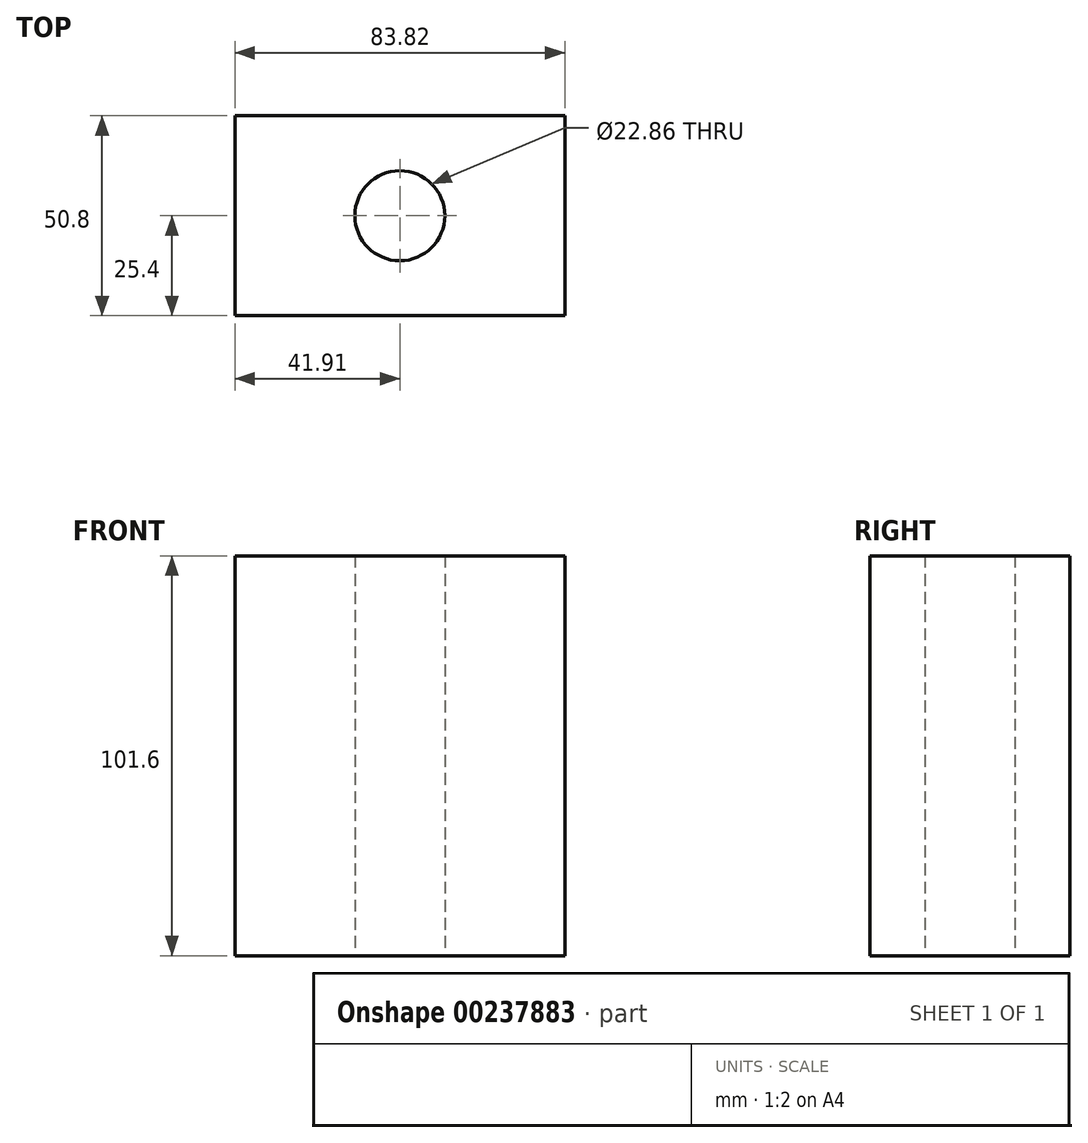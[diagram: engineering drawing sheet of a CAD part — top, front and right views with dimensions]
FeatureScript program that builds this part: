
annotation { "Feature Type Name" : "Feature", "Feature Type Description" : "" }
export const myFeature = defineFeature(function(context is Context, id is Id, definition is map)
    precondition{}
    {
        {
            var Q0;
            Q0=qCreatedBy(makeId("Top.planeOp"),FACE);
            var sketch = newSketch(context, id + "F0", { "sketchPlane" : qUnion([Q0])});
            skLineSegment(sketch, "E0.bottom", {"start": v(41.91, 25.4) * mm, "end": v(-41.9, 25.4) * mm});
            skLineSegment(sketch, "E0.top", {"start": v(41.91, -25.4) * mm, "end": v(-41.91, -25.4) * mm});
            skLineSegment(sketch, "E0.left", {"start": v(41.91, 25.4) * mm, "end": v(41.91, -25.4) * mm});
            skLineSegment(sketch, "E0.right", {"start": v(-41.9, 25.4) * mm, "end": v(-41.91, -25.4) * mm});
            skPoint(sketch, "E0.middle", {"position": v(0, 0) * mm});
            skCircle(sketch, "E1", {"center": v(0, 0) * mm, "radius": 11.43 * mm});
            skSolve(sketch);
        }
        {
            var Q0;
            Q0=makeQuery(id+"F0.imprint","IMPRINT",FACE,{"disambiguationData":[TD([[makeQuery(id+"F0.imprint","IMPRINT",EDGE,{"derivedFrom":sQuery(id+"F0.wireOp",EDGE,"E0.bottom")}),1.0]])]});
            extrude(context, id + "F1", {"entities" : qUnion([Q0]), "depth" : 101.6 * mm});
        }
    });
